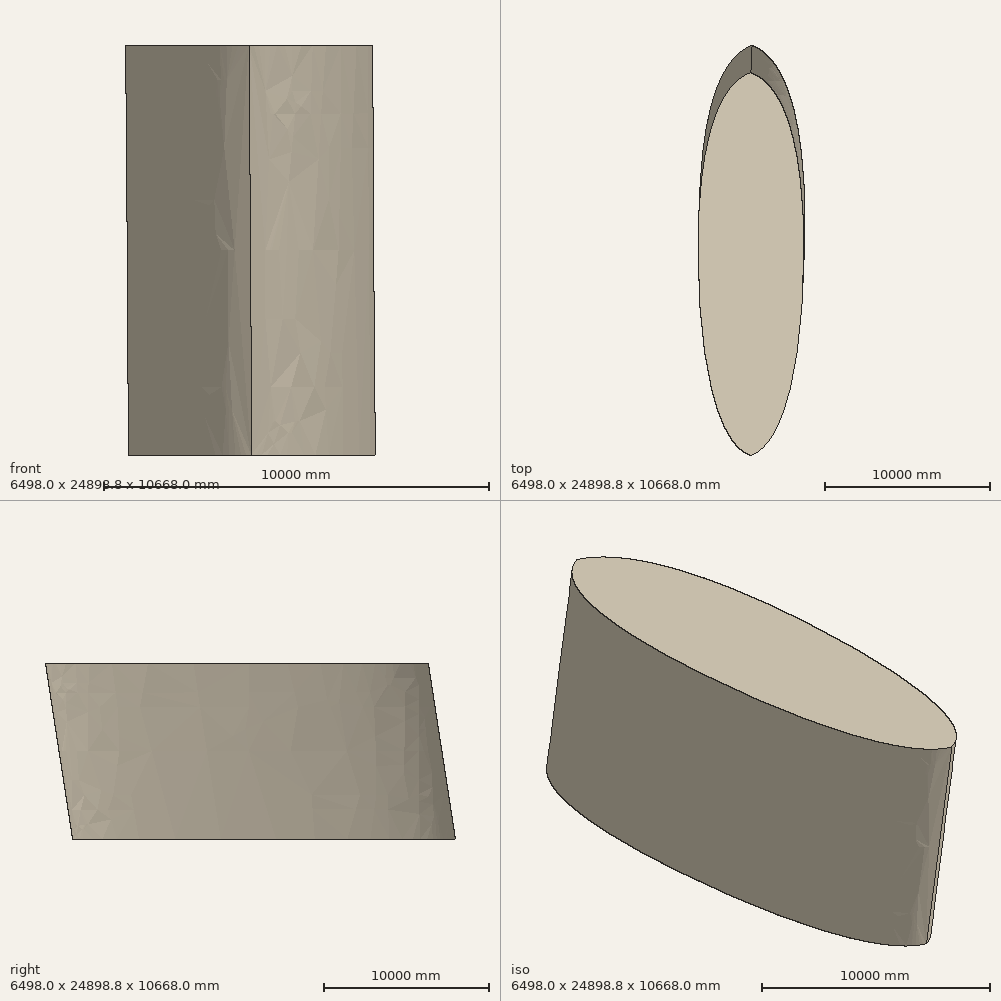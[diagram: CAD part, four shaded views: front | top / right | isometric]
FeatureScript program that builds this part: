
annotation { "Feature Type Name" : "Feature", "Feature Type Description" : "" }
export const myFeature = defineFeature(function(context is Context, id is Id, definition is map)
    precondition{}
    {
        {
            var Q0;
            Q0=qCreatedBy(makeId("Top.planeOp"),FACE);
            var sketch = newSketch(context, id + "F0", { "sketchPlane" : qUnion([Q0])});
            skFitSpline(sketch, "E0", {"points": [v(0, 11625) * mm, v(3205.8, 0) * mm, v(0, -11625) * mm], "startDerivative": vector(15522.95, -5939.48) * mm, "endDerivative": vector(-13295.83, -4387.36) * mm});
            skFitSpline(sketch, "E1.MirrorCS", {"points": [v(0, 11625) * mm, v(-3205.8, 0) * mm, v(0, -11625) * mm], "startDerivative": vector(-15522.95, -5939.48) * mm, "endDerivative": vector(13295.83, -4387.36) * mm});
            skSolve(sketch);
        }
        {
            var Q0;
            Q0=qCreatedBy(makeId("Top.planeOp"),FACE);
            cPlane(context, id + "F1", {"entities" : qUnion([Q0]), "cplaneType" : CPlaneType.OFFSET, "offset" : 10668 * mm, "width" : 152.4 * mm, "height" : 152.4 * mm});
        }
        {
            var Q0;
            Q0=qCreatedBy(id+"F1.planeOp",FACE);
            var sketch = newSketch(context, id + "F2", { "sketchPlane" : qUnion([Q0])});
            skFitSpline(sketch, "E2", {"points": [v(-70.73, 9976.17) * mm, v(3135.07, -1648.83) * mm, v(-70.73, -13273.83) * mm], "startDerivative": vector(15522.95, -5939.48) * mm, "endDerivative": vector(-13295.83, -4387.36) * mm});
            skFitSpline(sketch, "E3.MirrorCS", {"points": [v(-70.73, 9976.17) * mm, v(-3276.54, -1648.83) * mm, v(-70.73, -13273.83) * mm], "startDerivative": vector(-15522.95, -5939.48) * mm, "endDerivative": vector(13295.83, -4387.36) * mm});
            skSolve(sketch);
        }
        {
            var Q0;
            Q0=makeQuery(id+"F0.imprint","IMPRINT",FACE,{"disambiguationData":[TD([[makeQuery(id+"F0.imprint","IMPRINT",EDGE,{"derivedFrom":sQuery(id+"F0.wireOp",EDGE,"E0")}),-1.0]])]});
            var Q1;
            Q1=makeQuery(id+"F2.imprint","IMPRINT",FACE,{"disambiguationData":[TD([[makeQuery(id+"F2.imprint","IMPRINT",EDGE,{"derivedFrom":sQuery(id+"F2.wireOp",EDGE,"E2")}),-1.0]])]});
            loft(context, id + "F3", {"sheetProfilesArray" : [{ "sheetProfileEntities" : qUnion([Q0]) }, { "sheetProfileEntities" : qUnion([Q1]) }]});
        }
    });
